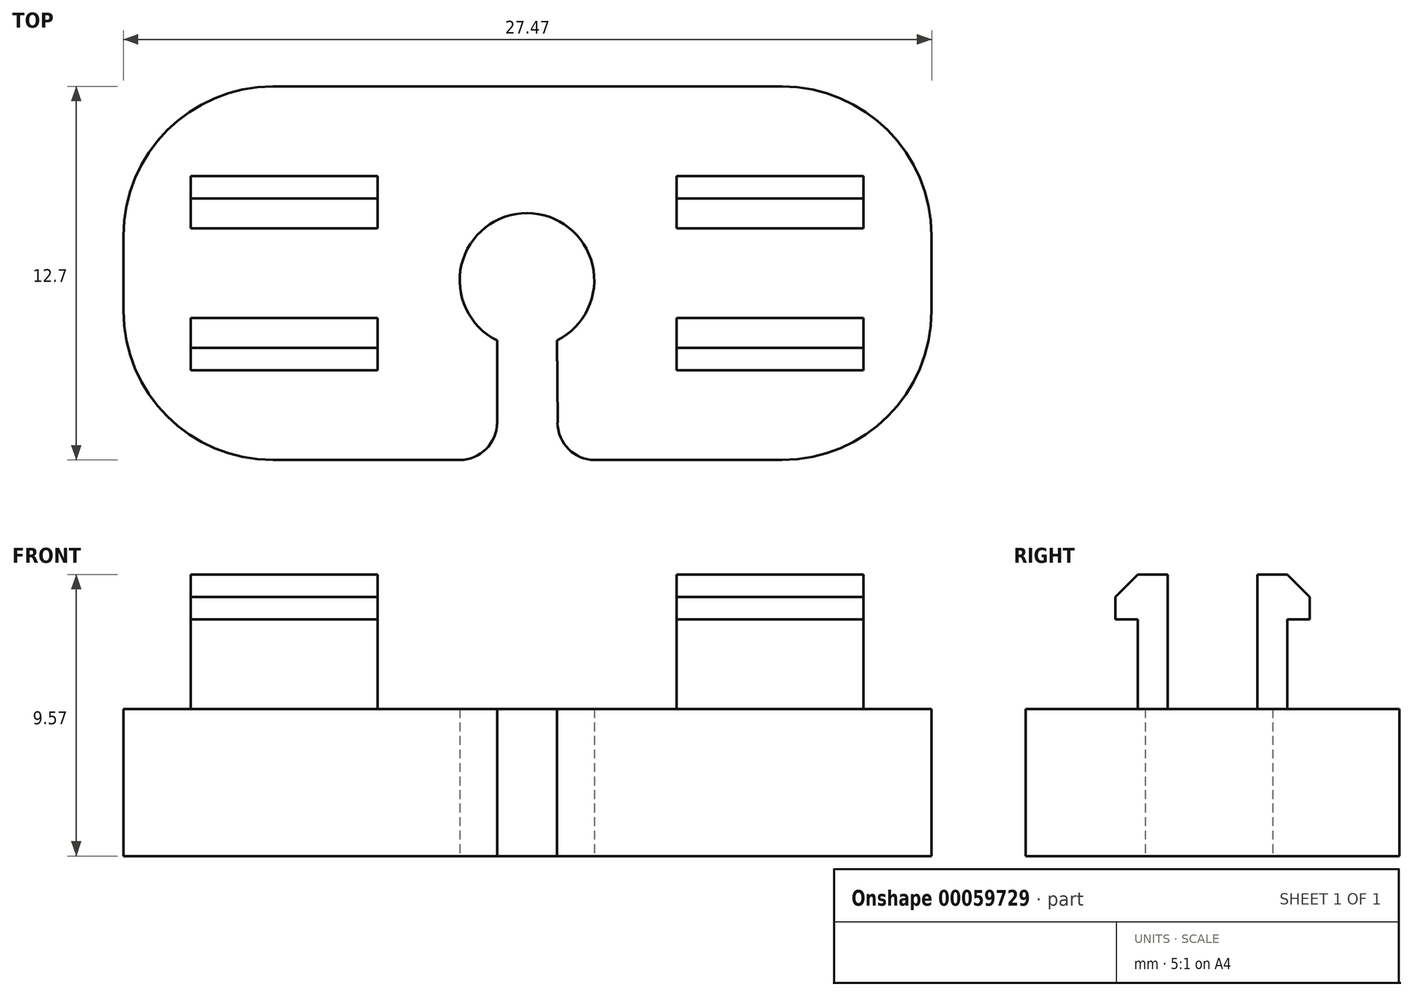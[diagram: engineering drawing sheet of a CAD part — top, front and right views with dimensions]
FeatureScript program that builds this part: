
annotation { "Feature Type Name" : "Feature", "Feature Type Description" : "" }
export const myFeature = defineFeature(function(context is Context, id is Id, definition is map)
    precondition{}
    {
        {
            var Q0;
            Q0=qCreatedBy(makeId("Top.planeOp"),FACE);
            var sketch = newSketch(context, id + "F0", { "sketchPlane" : qUnion([Q0])});
            skArc(sketch, "E0", {"start": v(1.08, 0) * mm, "mid": v(0.07, 4.33) * mm, "end": v(-0.95, 0) * mm});
            skLineSegment(sketch, "E1", {"start": v(-0.95, 0) * mm, "end": v(-0.95, -4.06) * mm});
            skLineSegment(sketch, "E2", {"start": v(-0.95, -4.06) * mm, "end": v(-13.65, -4.06) * mm});
            skLineSegment(sketch, "E3", {"start": v(-13.65, -4.06) * mm, "end": v(-13.65, 8.64) * mm});
            skLineSegment(sketch, "E4", {"start": v(-13.65, 8.64) * mm, "end": v(13.82, 8.64) * mm});
            skLineSegment(sketch, "E5", {"start": v(13.82, 8.64) * mm, "end": v(13.82, -4.06) * mm});
            skLineSegment(sketch, "E6", {"start": v(13.82, -4.06) * mm, "end": v(1.12, -4.06) * mm});
            skLineSegment(sketch, "E7", {"start": v(1.12, -4.06) * mm, "end": v(1.08, 0) * mm});
            skLineSegment(sketch, "E8", {"start": v(-13.65, 2.29) * mm, "end": v(13.82, 2.29) * mm, "construction": true});
            skCircle(sketch, "E9", {"center": v(-9.59, 2.29) * mm, "radius": 2.29 * mm, "construction": true});
            skCircle(sketch, "E10", {"center": v(9.75, 2.29) * mm, "radius": 2.29 * mm, "construction": true});
            skSolve(sketch);
        }
        {
            var Q0;
            Q0 = qSketchRegion(id + "F0", true);
            extrude(context, id + "F1", {"entities" : qUnion([Q0]), "depth" : 5 * mm});
        }
        {
            var Q0;
            Q0=makeQuery(id+"F1.opExtrude","SWEPT_EDGE",EDGE,{"disambiguationData":[OSD([sQuery(id+"F0.wireOp",EDGE,"E3"),sQuery(id+"F0.wireOp",EDGE,"E4")])]});
            var Q1;
            Q1=makeQuery(id+"F1.opExtrude","SWEPT_EDGE",EDGE,{"disambiguationData":[OSD([sQuery(id+"F0.wireOp",EDGE,"E4"),sQuery(id+"F0.wireOp",EDGE,"E5")])]});
            var Q2;
            Q2=makeQuery(id+"F1.opExtrude","SWEPT_EDGE",EDGE,{"disambiguationData":[OSD([sQuery(id+"F0.wireOp",EDGE,"E5"),sQuery(id+"F0.wireOp",EDGE,"E6")])]});
            var Q3;
            Q3=makeQuery(id+"F1.opExtrude","SWEPT_EDGE",EDGE,{"disambiguationData":[OSD([sQuery(id+"F0.wireOp",EDGE,"E2"),sQuery(id+"F0.wireOp",EDGE,"E3")])]});
            fillet(context, id + "F2", {"entities" : qUnion([Q0, Q1, Q2, Q3]), "radius" : 5.08 * mm, "tangentPropagation" : true, "allowEdgeOverflow" : false});
        }
        {
            var Q0;
            Q0=makeQuery(id+"F1.opExtrude","SWEPT_EDGE",EDGE,{"disambiguationData":[OSD([sQuery(id+"F0.wireOp",EDGE,"E6"),sQuery(id+"F0.wireOp",EDGE,"E7")])]});
            var Q1;
            Q1=makeQuery(id+"F1.opExtrude","SWEPT_EDGE",EDGE,{"disambiguationData":[OSD([sQuery(id+"F0.wireOp",EDGE,"E1"),sQuery(id+"F0.wireOp",EDGE,"E2")])]});
            fillet(context, id + "F3", {"entities" : qUnion([Q0, Q1]), "radius" : 1.27 * mm, "tangentPropagation" : true, "allowEdgeOverflow" : false});
        }
        {
            var Q0;
            Q0=makeQuery(id+"F1.opExtrude","CAP_FACE",FACE,{"disambiguationData":[OSD([sQuery(id+"F0.wireOp",EDGE,"E0"),sQuery(id+"F0.wireOp",EDGE,"E1"),sQuery(id+"F0.wireOp",EDGE,"E2"),sQuery(id+"F0.wireOp",EDGE,"E3"),sQuery(id+"F0.wireOp",EDGE,"E4"),sQuery(id+"F0.wireOp",EDGE,"E5"),sQuery(id+"F0.wireOp",EDGE,"E6"),sQuery(id+"F0.wireOp",EDGE,"E7")])],"isStart":false});
            var sketch = newSketch(context, id + "F4", { "sketchPlane" : qUnion([Q0])});
            skLineSegment(sketch, "E11.bottom", {"start": v(-11.36, 0.76) * mm, "end": v(-5.01, 0.76) * mm});
            skLineSegment(sketch, "E11.top", {"start": v(-11.36, -0.25) * mm, "end": v(-5.01, -0.25) * mm});
            skLineSegment(sketch, "E11.left", {"start": v(-11.36, 0.76) * mm, "end": v(-11.36, -0.25) * mm});
            skLineSegment(sketch, "E11.right", {"start": v(-5.01, 0.76) * mm, "end": v(-5.01, -0.25) * mm});
            skPoint(sketch, "E12.firstSnap0", {"position": v(-11.36, 0.25) * mm});
            skLineSegment(sketch, "E12.bottom", {"start": v(-11.36, 3.8) * mm, "end": v(-5.01, 3.8) * mm});
            skLineSegment(sketch, "E12.top", {"start": v(-11.36, 4.83) * mm, "end": v(-5.01, 4.83) * mm});
            skLineSegment(sketch, "E12.left", {"start": v(-11.36, 3.8) * mm, "end": v(-11.36, 4.83) * mm});
            skLineSegment(sketch, "E12.right", {"start": v(-5.01, 3.8) * mm, "end": v(-5.01, 4.83) * mm});
            skLineSegment(sketch, "E13.bottom", {"start": v(5.15, 4.83) * mm, "end": v(11.5, 4.83) * mm});
            skLineSegment(sketch, "E13.top", {"start": v(5.15, 3.8) * mm, "end": v(11.5, 3.8) * mm});
            skLineSegment(sketch, "E13.left", {"start": v(5.15, 4.83) * mm, "end": v(5.15, 3.8) * mm});
            skLineSegment(sketch, "E13.right", {"start": v(11.5, 4.83) * mm, "end": v(11.5, 3.8) * mm});
            skLineSegment(sketch, "E14.bottom", {"start": v(5.15, 0.76) * mm, "end": v(11.5, 0.76) * mm});
            skLineSegment(sketch, "E14.top", {"start": v(5.15, -0.25) * mm, "end": v(11.5, -0.25) * mm});
            skLineSegment(sketch, "E14.left", {"start": v(5.15, 0.76) * mm, "end": v(5.15, -0.25) * mm});
            skLineSegment(sketch, "E14.right", {"start": v(11.5, 0.76) * mm, "end": v(11.5, -0.25) * mm});
            skLineSegment(sketch, "E15", {"start": v(-13.65, 2.29) * mm, "end": v(13.82, 2.29) * mm, "construction": true});
            skLineSegment(sketch, "E16", {"start": v(0.07, 8.64) * mm, "end": v(0.07, -4.02) * mm, "construction": true});
            skPoint(sketch, "E16.startSnap0", {"position": v(0.07, 4.33) * mm});
            skSolve(sketch);
        }
        {
            var Q0;
            Q0 = qSketchRegion(id + "F4", true);
            extrude(context, id + "F5", {"entities" : qUnion([Q0]), "operationType" : NewBodyOperationType.ADD, "depth" : 3.05 * mm});
        }
        {
            var Q0;
            Q0=makeQuery(id+"F5.opExtrude","CAP_FACE",FACE,{"disambiguationData":[OSD([sQuery(id+"F4.wireOp",EDGE,"E12.bottom"),sQuery(id+"F4.wireOp",EDGE,"E12.top"),sQuery(id+"F4.wireOp",EDGE,"E12.left"),sQuery(id+"F4.wireOp",EDGE,"E12.right")])],"isStart":false});
            var sketch = newSketch(context, id + "F6", { "sketchPlane" : qUnion([Q0])});
            skLineSegment(sketch, "E17.bottom", {"start": v(-11.36, 3.8) * mm, "end": v(-5.01, 3.8) * mm});
            skLineSegment(sketch, "E17.top", {"start": v(-11.36, 5.59) * mm, "end": v(-5.01, 5.59) * mm});
            skLineSegment(sketch, "E17.left", {"start": v(-11.36, 3.8) * mm, "end": v(-11.36, 5.59) * mm});
            skLineSegment(sketch, "E17.right", {"start": v(-5.01, 3.8) * mm, "end": v(-5.01, 5.59) * mm});
            skLineSegment(sketch, "E18.bottom", {"start": v(-11.36, 0.76) * mm, "end": v(-5.01, 0.76) * mm});
            skLineSegment(sketch, "E18.top", {"start": v(-11.36, -1.02) * mm, "end": v(-5.01, -1.02) * mm});
            skLineSegment(sketch, "E18.left", {"start": v(-11.36, 0.76) * mm, "end": v(-11.36, -1.02) * mm});
            skLineSegment(sketch, "E18.right", {"start": v(-5.01, 0.76) * mm, "end": v(-5.01, -1.02) * mm});
            skLineSegment(sketch, "E19.bottom", {"start": v(5.15, 3.8) * mm, "end": v(11.5, 3.8) * mm});
            skLineSegment(sketch, "E19.top", {"start": v(5.15, 5.59) * mm, "end": v(11.5, 5.59) * mm});
            skLineSegment(sketch, "E19.left", {"start": v(5.15, 3.8) * mm, "end": v(5.15, 5.59) * mm});
            skLineSegment(sketch, "E19.right", {"start": v(11.5, 3.8) * mm, "end": v(11.5, 5.59) * mm});
            skLineSegment(sketch, "E20.bottom", {"start": v(5.15, 0.76) * mm, "end": v(11.5, 0.76) * mm});
            skLineSegment(sketch, "E20.top", {"start": v(5.15, -1.02) * mm, "end": v(11.5, -1.02) * mm});
            skLineSegment(sketch, "E20.left", {"start": v(5.15, 0.76) * mm, "end": v(5.15, -1.02) * mm});
            skLineSegment(sketch, "E20.right", {"start": v(11.5, 0.76) * mm, "end": v(11.5, -1.02) * mm});
            skSolve(sketch);
        }
        {
            var Q0;
            Q0 = qSketchRegion(id + "F6", true);
            extrude(context, id + "F7", {"entities" : qUnion([Q0]), "operationType" : NewBodyOperationType.ADD, "depth" : 1.52 * mm});
        }
        {
            var Q0;
            Q0=makeQuery(id+"F7.opExtrude","CAP_EDGE",EDGE,{"disambiguationData":[OSD([sQuery(id+"F6.wireOp",EDGE,"E18.top")])],"isStart":false});
            var Q1;
            Q1=makeQuery(id+"F7.opExtrude","CAP_EDGE",EDGE,{"disambiguationData":[OSD([sQuery(id+"F6.wireOp",EDGE,"E17.top")])],"isStart":false});
            var Q2;
            Q2=makeQuery(id+"F7.opExtrude","CAP_EDGE",EDGE,{"disambiguationData":[OSD([sQuery(id+"F6.wireOp",EDGE,"E19.top")])],"isStart":false});
            var Q3;
            Q3=makeQuery(id+"F7.opExtrude","CAP_EDGE",EDGE,{"disambiguationData":[OSD([sQuery(id+"F6.wireOp",EDGE,"E20.top")])],"isStart":false});
            chamfer(context, id + "F8", {"entities" : qUnion([Q0, Q1, Q2, Q3]), "width" : 0.76 * mm, "tangentPropagation" : true});
        }
    });
